# Revit family: Haworth_Hobo_Bench
name_source: partatom
category: Furniture
revit_build: Autodesk Revit 2018 (Build: 20170223_1515(x64)
units: mm (PartAtom-declared; Revit-internal decimal feet)

## family parameters
Always vertical = Yes
Cut with Voids When Loaded = No
OmniClass Number = 23.40.70.14.64.21
OmniClass Title = Systems Furniture
Room Calculation Point = No
Shared = No
Work Plane-Based = No

## types (2) — shared parameters
Actual Depth = 27 1/2"
Actual Height = 16 1/2"
Assembly Code = E2020200
Leg Offset = 4 235/256"
Manufacturer = Haworth
Model = HCCE-HBB
Revision Number = 1
Size = Verify Final Dim. w/ Haworth
URL = http://www.haworth.com
URL - Product = https://www.haworth.com
Warranty = http://www.haworth.com

## per-type parameters (varying)
| type | Actual Width | Description | One Seat | Two Seats |
| HCCE-HBB2 - Two Seats Bench | 63" | Haworth Hobo Two Seats Bench | No | Yes |
| HCCE-HBB1 - One Seat Bench | 31 1/2" | Haworth Hobo One Seat Bench | Yes | No |

## geometry (parser evidence)
native form markers: Extrusion x2, Sweep x6
no freeform markers — native parametric forms only
